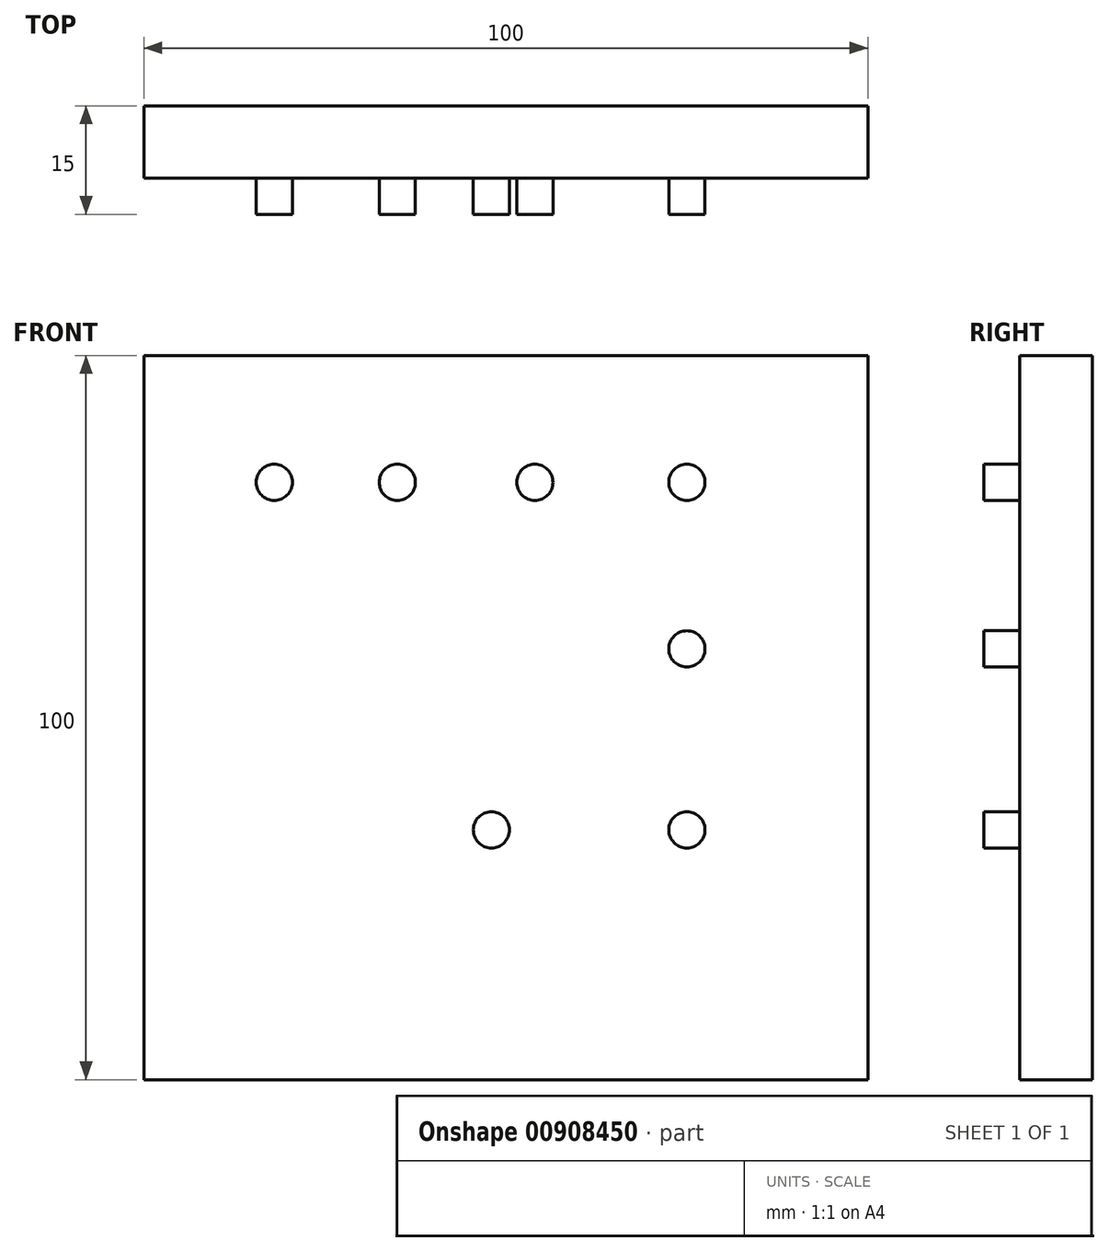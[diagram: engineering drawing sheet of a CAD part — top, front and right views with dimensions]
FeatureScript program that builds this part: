
annotation { "Feature Type Name" : "Feature", "Feature Type Description" : "" }
export const myFeature = defineFeature(function(context is Context, id is Id, definition is map)
    precondition{}
    {
        {
            var Q0;
            Q0=qCreatedBy(makeId("Front.planeOp"),FACE);
            var sketch = newSketch(context, id + "F0", { "sketchPlane" : qUnion([Q0])});
            skLineSegment(sketch, "E0.bottom", {"start": v(0, 0) * mm, "end": v(100, 0) * mm});
            skLineSegment(sketch, "E0.top", {"start": v(0, 100) * mm, "end": v(100, 100) * mm});
            skLineSegment(sketch, "E0.left", {"start": v(0, 0) * mm, "end": v(0, 100) * mm});
            skLineSegment(sketch, "E0.right", {"start": v(100, 0) * mm, "end": v(100, 100) * mm});
            skCircle(sketch, "E1", {"center": v(12, 81.87) * mm, "radius": 2.5 * mm});
            skCircle(sketch, "E2", {"center": v(29, 81.87) * mm, "radius": 2.5 * mm});
            skCircle(sketch, "E3", {"center": v(48, 81.87) * mm, "radius": 2.5 * mm});
            skCircle(sketch, "E4", {"center": v(69, 81.87) * mm, "radius": 2.5 * mm});
            skSolve(sketch);
        }
        {
            var Q0;
            Q0=makeQuery(id+"F0.imprint","IMPRINT",FACE,{"disambiguationData":[TD([[makeQuery(id+"F0.imprint","IMPRINT",EDGE,{"derivedFrom":sQuery(id+"F0.wireOp",EDGE,"E0.bottom")}),1.0]])]});
            var Q1;
            Q1=makeQuery(id+"F0.imprint","IMPRINT",FACE,{"disambiguationData":[TD([[makeQuery(id+"F0.imprint","IMPRINT",EDGE,{"derivedFrom":sQuery(id+"F0.wireOp",EDGE,"E1")}),1.0]])]});
            var Q2;
            Q2=makeQuery(id+"F0.imprint","IMPRINT",FACE,{"disambiguationData":[TD([[makeQuery(id+"F0.imprint","IMPRINT",EDGE,{"derivedFrom":sQuery(id+"F0.wireOp",EDGE,"E2")}),1.0]])]});
            var Q3;
            Q3=makeQuery(id+"F0.imprint","IMPRINT",FACE,{"disambiguationData":[TD([[makeQuery(id+"F0.imprint","IMPRINT",EDGE,{"derivedFrom":sQuery(id+"F0.wireOp",EDGE,"E3")}),1.0]])]});
            var Q4;
            Q4=makeQuery(id+"F0.imprint","IMPRINT",FACE,{"disambiguationData":[TD([[makeQuery(id+"F0.imprint","IMPRINT",EDGE,{"derivedFrom":sQuery(id+"F0.wireOp",EDGE,"E4")}),1.0]])]});
            extrude(context, id + "F1", {"entities" : qUnion([Q0, Q1, Q2, Q3, Q4]), "depth" : 10 * mm, "offsetDistance" : 25 * mm});
        }
        {
            var Q0;
            Q0=makeQuery(id+"F1.opExtrude","CAP_FACE",FACE,{"disambiguationData":[OSD([sQuery(id+"F0.wireOp",EDGE,"E0.bottom"),sQuery(id+"F0.wireOp",EDGE,"E0.top"),sQuery(id+"F0.wireOp",EDGE,"E0.left"),sQuery(id+"F0.wireOp",EDGE,"E0.right")])],"isStart":false});
            var sketch = newSketch(context, id + "F2", { "sketchPlane" : qUnion([Q0])});
            skCircle(sketch, "E5", {"center": v(18, 82.5) * mm, "radius": 2.5 * mm});
            skCircle(sketch, "E6", {"center": v(35, 82.5) * mm, "radius": 2.5 * mm});
            skCircle(sketch, "E7", {"center": v(54, 82.5) * mm, "radius": 2.5 * mm});
            skCircle(sketch, "E8", {"center": v(75, 82.5) * mm, "radius": 2.5 * mm});
            skCircle(sketch, "E9", {"center": v(75, 59.5) * mm, "radius": 2.5 * mm});
            skCircle(sketch, "E10", {"center": v(75, 34.5) * mm, "radius": 2.5 * mm});
            skCircle(sketch, "E11", {"center": v(48, 34.5) * mm, "radius": 2.5 * mm});
            skSolve(sketch);
        }
        {
            var Q0;
            Q0=makeQuery(id+"F2.imprint","IMPRINT",FACE,{"disambiguationData":[TD([[makeQuery(id+"F2.imprint","IMPRINT",EDGE,{"derivedFrom":sQuery(id+"F2.wireOp",EDGE,"E5")}),1.0]])]});
            var Q1;
            Q1=makeQuery(id+"F2.imprint","IMPRINT",FACE,{"disambiguationData":[TD([[makeQuery(id+"F2.imprint","IMPRINT",EDGE,{"derivedFrom":sQuery(id+"F2.wireOp",EDGE,"E6")}),1.0]])]});
            var Q2;
            Q2=makeQuery(id+"F2.imprint","IMPRINT",FACE,{"disambiguationData":[TD([[makeQuery(id+"F2.imprint","IMPRINT",EDGE,{"derivedFrom":sQuery(id+"F2.wireOp",EDGE,"E7")}),1.0]])]});
            var Q3;
            Q3=makeQuery(id+"F2.imprint","IMPRINT",FACE,{"disambiguationData":[TD([[makeQuery(id+"F2.imprint","IMPRINT",EDGE,{"derivedFrom":sQuery(id+"F2.wireOp",EDGE,"E8")}),1.0]])]});
            var Q4;
            Q4=makeQuery(id+"F2.imprint","IMPRINT",FACE,{"disambiguationData":[TD([[makeQuery(id+"F2.imprint","IMPRINT",EDGE,{"derivedFrom":sQuery(id+"F2.wireOp",EDGE,"E9")}),1.0]])]});
            var Q5;
            Q5=makeQuery(id+"F2.imprint","IMPRINT",FACE,{"disambiguationData":[TD([[makeQuery(id+"F2.imprint","IMPRINT",EDGE,{"derivedFrom":sQuery(id+"F2.wireOp",EDGE,"E10")}),1.0]])]});
            var Q6;
            Q6=makeQuery(id+"F2.imprint","IMPRINT",FACE,{"disambiguationData":[TD([[makeQuery(id+"F2.imprint","IMPRINT",EDGE,{"derivedFrom":sQuery(id+"F2.wireOp",EDGE,"E11")}),1.0]])]});
            extrude(context, id + "F3", {"entities" : qUnion([Q0, Q1, Q2, Q3, Q4, Q5, Q6]), "operationType" : NewBodyOperationType.ADD, "depth" : 5 * mm, "offsetDistance" : 25 * mm});
        }
    });
